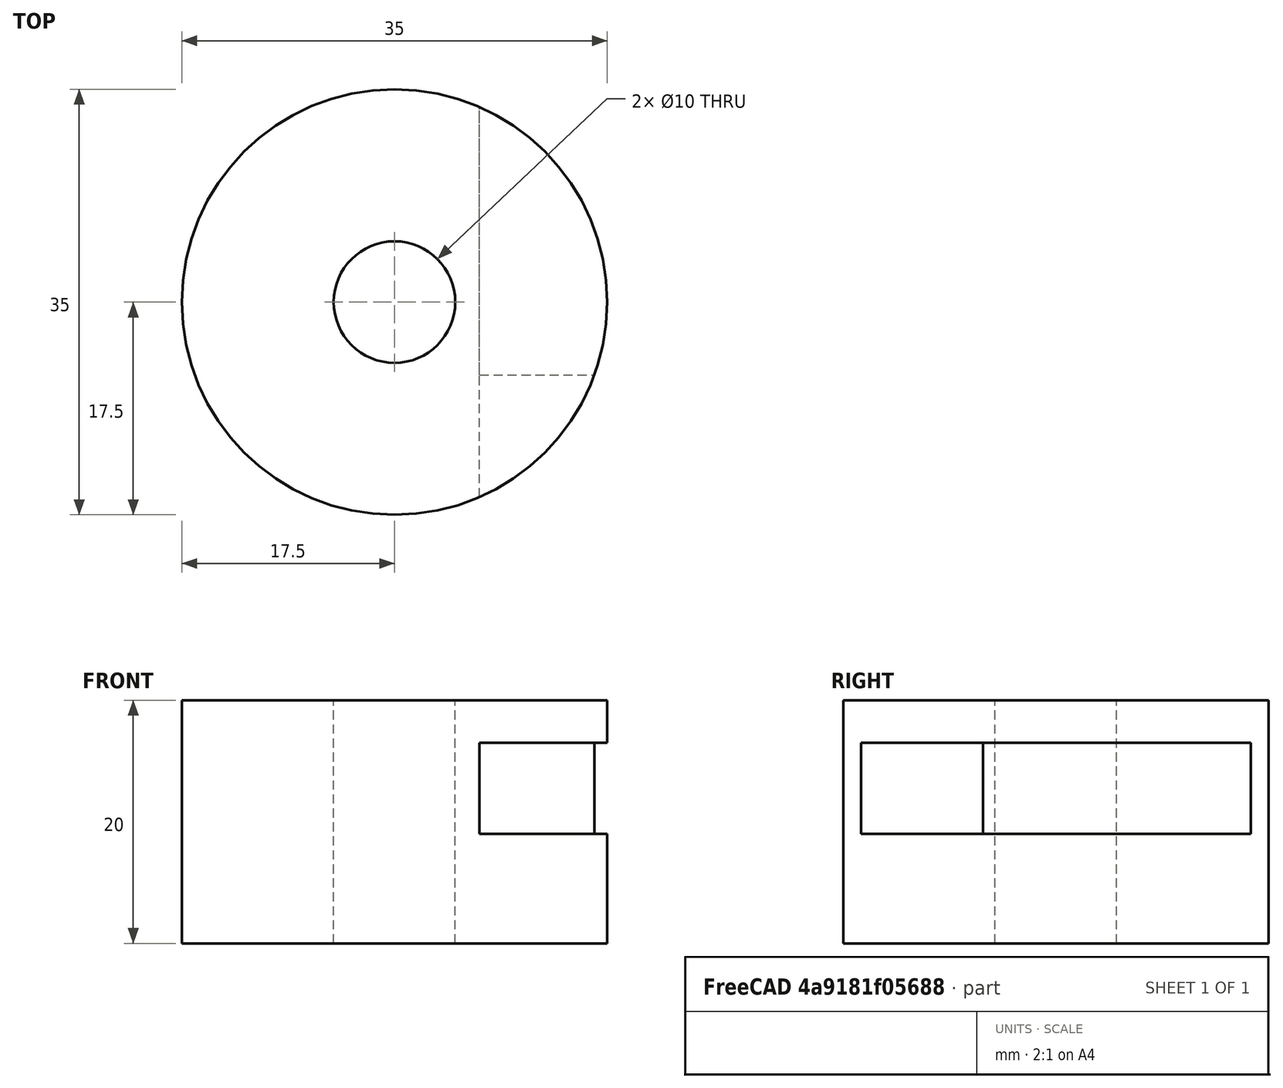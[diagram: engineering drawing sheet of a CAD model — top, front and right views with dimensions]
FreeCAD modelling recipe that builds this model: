
FCSTD DOCUMENT  (FreeCAD 0.15R4671 (Git))
Label: sign-with-hardware
License: All rights reserved
LicenseURL: http://en.wikipedia.org/wiki/All_rights_reserved
objects: Drawing::FeatureView×8, Drawing::FeatureViewPart×6, Part::Cylinder×4, Part::Cut×4, Part::Box×2, Drawing::FeaturePage×1, Mesh::Feature×1
note: 10 computed .brp shape members not serialized (recipe doc carries the construction recipe); baked Part::Feature solids carry a one-line shape summary decoded from their .brp

FEATURE [Part::Cylinder] Cylinder
  Angle = 360
  Height = 20
  Radius = 17.5
FEATURE [Part::Cylinder] Cylinder001
  Angle = 360
  Height = 40
  Placement = pos=(0,0,-10) rot=(0,0,1;0rad)
  Radius = 5
FEATURE [Part::Cut] Cut
  Base = -> Cylinder
  Tool = -> Cylinder001
FEATURE [Part::Box] Box  label="Cube"
  Height = 7.5
  Length = 30
  Placement = pos=(7,-6,9) rot=(0,0,1;0rad)
  Width = 30
FEATURE [Part::Cut] Cut001  label="Mount (Bottom)"
  Base = -> Cut
  Tool = -> Box
FEATURE [Part::Cylinder] Cylinder002
  Angle = 360
  Height = 20
  Radius = 17.5
FEATURE [Part::Cylinder] Cylinder003
  Angle = 360
  Height = 40
  Placement = pos=(0,0,-10) rot=(0,0,1;0rad)
  Radius = 5
FEATURE [Part::Cut] Cut002
  Base = -> Cylinder002
  Tool = -> Cylinder003
FEATURE [Part::Box] Box001  label="Cube001"
  Height = 7.5
  Length = 30
  Placement = pos=(7,-20,9) rot=(0,0,1;0rad)
  Width = 70
FEATURE [Part::Cut] Cut003  label="Mount (Top)"
  Base = -> Cut002
  Tool = -> Box001
FEATURE [Drawing::FeatureViewPart] View  label="Bottom - Front"
  Direction = (0,0,1)
  HiddenWidth = 0.15
  LineWidth = 0.35
  Rotation = 0
  ShowHiddenLines = true
  ShowSmoothLines = false
  Source = -> Cut001
  Tolerance = 0.05
  ViewResult = <g id="Bottom - Front"\n   transform="rotate(0,70,50) translate(70,50) scale(1,1)"\n  >\n<g   stroke="rgb(0, 0, 0)"\n   stroke-width="0.15"\n   stroke-linecap="butt"\n   stroke-linejoin="miter"\n   stroke-dasharray="0.2,0.1"\n   fill="none"\n   transform="scale(1,-1)"\n  >\n<path d="M16.4393 -6 A17.5 17.5 0 0 1 17.5 -4.28626e-015" /><path d="M16.4393 -6 A17.5 17.5 0 0 1 17.5 -4.28626e-015" /><circle cx ="0" cy ="0" r ="17.5" /><path d="M17.5 0 A17.5 17.5 0 0 1 7 16.039" /><path d="M17.5 0 A17.5 17.5 0 0 1 7 16.039" /><path id= "6" d=" M 7 -6 L 7 16.039 " />\n<path id= "7" d=" M 7 -6 L 16.4393 -6 " />\n<path id= "8" d=" M 7 -6 L 16.4393 -6 " />\n<path id= "9" d=" M 7 -6 L 7 16.039 " />\n<circle cx ="0" cy ="0" r ="5" /></g>\n<g   stroke="rgb(0, 0, 0)"\n   stroke-width="0.35"\n   stroke-linecap="butt"\n   stroke-linejoin="miter"\n   fill="none"\n   transform="scale(1,-1)"\n  >\n<circle cx ="0" cy ="0" r ="17.5" /><circle cx ="0" cy ="0" r ="5" /></g>\n</g>
  Visible = true
  X = 70
  Y = 50
FEATURE [Drawing::FeatureViewPart] View001  label="Top - Front"
  Direction = (0,0,1)
  HiddenWidth = 0.15
  LineWidth = 0.35
  Rotation = 0
  ShowHiddenLines = true
  ShowSmoothLines = false
  Source = -> Cut003
  Tolerance = 0.05
  ViewResult = <g id="Top - Front"\n   transform="rotate(0,70,120) translate(70,120) scale(1,1)"\n  >\n<g   stroke="rgb(0, 0, 0)"\n   stroke-width="0.15"\n   stroke-linecap="butt"\n   stroke-linejoin="miter"\n   stroke-dasharray="0.2,0.1"\n   fill="none"\n   transform="scale(1,-1)"\n  >\n<path d="M7 -16.039 A17.5 17.5 0 0 1 17.5 -4.28626e-015" /><path d="M7 -16.039 A17.5 17.5 0 0 1 17.5 -4.28626e-015" /><circle cx ="0" cy ="0" r ="17.5" /><path d="M17.5 0 A17.5 17.5 0 0 1 7 16.039" /><path d="M17.5 0 A17.5 17.5 0 0 1 7 16.039" /><path id= "6" d=" M 7 -16.039 L 7 16.039 " />\n<path id= "7" d=" M 7 -16.039 L 7 16.039 " />\n<circle cx ="0" cy ="0" r ="5" /></g>\n<g   stroke="rgb(0, 0, 0)"\n   stroke-width="0.35"\n   stroke-linecap="butt"\n   stroke-linejoin="miter"\n   fill="none"\n   transform="scale(1,-1)"\n  >\n<circle cx ="0" cy ="0" r ="17.5" /><circle cx ="0" cy ="0" r ="5" /></g>\n</g>
  Visible = true
  X = 70
  Y = 120
FEATURE [Drawing::FeatureViewPart] View002  label="Top - Side"
  Direction = (1,0,0)
  HiddenWidth = 0.15
  LineWidth = 0.35
  Rotation = 180
  ShowHiddenLines = true
  ShowSmoothLines = false
  Source = -> Cut003
  Tolerance = 0.05
  ViewResult = <blob: 4388 chars omitted>
  Visible = true
  X = 160
  Y = 120
FEATURE [Drawing::FeatureViewPart] View003  label="Bottom - Side"
  Direction = (1,0,0)
  HiddenWidth = 0.15
  LineWidth = 0.35
  Rotation = 180
  ShowHiddenLines = false
  ShowSmoothLines = false
  Source = -> Cut001
  Tolerance = 0.05
  ViewResult = <blob: 2232 chars omitted>
  Visible = true
  X = 160
  Y = 50
FEATURE [Drawing::FeatureViewPart] View004  label="Bottom - Ortho"
  Direction = (1,1,1)
  HiddenWidth = 0.15
  LineWidth = 0.35
  Rotation = 0
  ShowHiddenLines = false
  ShowSmoothLines = false
  Source = -> Cut001
  Tolerance = 0.05
  ViewResult = <g id="Bottom - Ortho"\n   transform="rotate(0,240,45) translate(240,45) scale(1,1)"\n  >\n<g   stroke="rgb(0, 0, 0)"\n   stroke-width="0.35"\n   stroke-linecap="butt"\n   stroke-linejoin="miter"\n   fill="none"\n   transform="scale(1,-1)"\n  >\n<path id= "1" d=" M -8.75 15.1554 L -22.8921 6.99048 " />\n<path id= "2" d=" M 8.75 -15.1554 L -5.39214 -23.3204 " />\n</g>\n<g   stroke="rgb(0, 0, 0)"\n   stroke-width="0.35"\n   stroke-linecap="butt"\n   stroke-linejoin="miter"\n   fill="none"\n   transform="scale(1,-1)"\n  >\n<path d="M-0.042934 -18.3464 A17.5 10.1036 120 0 1 0.707107 -13.8804" />\n<path id= "2" d=" M 5.26037 -15.2845 L -0.042934 -18.3464 " />\n<path d="M5.26037 -15.2845 A17.5 10.1036 120 0 1 6.01041 -10.8186" />\n<path d="M12.3744 -7.14435 A17.5 10.1036 120 0 1 -8.75 15.1554" />\n<path d="M8.75 -15.1554 A17.5 10.1036 120 0 1 12.3744 -7.14435" />\n<path d="M6.01041 -10.8186 A17.5 10.1036 120 0 1 -1.41421 6.56383" />\n<path id= "7" d=" M -1.41421 6.56383 L -6.71751 3.50197 " />\n<path d="M0.707107 -13.8804 A17.5 10.1036 120 0 1 -6.71751 3.50197" />\n<path d="M-1.76777 -15.3093 A17.5 10.1036 120 0 1 -22.8921 6.99048" />\n<path d="M-22.8921 6.99048 A17.5 10.1036 120 0 1 -5.39214 -23.3204" />\n<path d="M-5.39214 -23.3204 A17.5 10.1036 120 0 1 -1.76777 -15.3093" />\n<path id= "12" d=" M 0.661566 -12.6294 L 5.26037 -15.2845 " />\n<path id= "13" d=" M -1.41421 -4.6557 L -1.41421 6.56383 " />\n<path d="M-10.6066 -10.2062 A5 2.88675 120 0 1 -16.6421 -3.83484" />\n<path d="M-16.6421 -3.83484 A5 2.88675 120 0 1 -11.6421 -12.4951" />\n<path d="M-11.6421 -12.4951 A5 2.88675 120 0 1 -10.6066 -10.2062" />\n</g>\n</g>
  Visible = true
  X = 240
  Y = 45
FEATURE [Drawing::FeatureViewPart] View005  label="Top - Ortho"
  Direction = (1,1,1)
  HiddenWidth = 0.15
  LineWidth = 0.35
  Rotation = 0
  ShowHiddenLines = false
  ShowSmoothLines = false
  Source = -> Cut003
  Tolerance = 0.05
  ViewResult = <g id="Top - Ortho"\n   transform="rotate(0,240,115) translate(240,115) scale(1,1)"\n  >\n<g   stroke="rgb(0, 0, 0)"\n   stroke-width="0.35"\n   stroke-linecap="butt"\n   stroke-linejoin="miter"\n   fill="none"\n   transform="scale(1,-1)"\n  >\n<path id= "1" d=" M -8.75 15.1554 L -22.8921 6.99048 " />\n<path id= "2" d=" M 8.75 -15.1554 L 2.38604 -18.8297 " />\n<path id= "3" d=" M -2.91726 -21.8915 L -5.39214 -23.3204 " />\n</g>\n<g   stroke="rgb(0, 0, 0)"\n   stroke-width="0.35"\n   stroke-linecap="butt"\n   stroke-linejoin="miter"\n   fill="none"\n   transform="scale(1,-1)"\n  >\n<path d="M-2.91726 -21.8915 A17.5 10.1036 120 0 1 0.707107 -13.8804" />\n<path d="M-0.677071 -19.6479 A17.5 10.1036 120 0 1 2.38604 -18.8297" />\n<path d="M2.38604 -18.8297 A17.5 10.1036 120 0 1 6.01041 -10.8186" />\n<path d="M12.3744 -7.14435 A17.5 10.1036 120 0 1 -8.75 15.1554" />\n<path d="M8.75 -15.1554 A17.5 10.1036 120 0 1 12.3744 -7.14435" />\n<path d="M6.01041 -10.8186 A17.5 10.1036 120 0 1 -1.41421 6.56383" />\n<path id= "7" d=" M -1.41421 6.56383 L -6.71751 3.50197 " />\n<path d="M0.707107 -13.8804 A17.5 10.1036 120 0 1 -6.71751 3.50197" />\n<path d="M-1.76777 -15.3093 A17.5 10.1036 120 0 1 -22.8921 6.99048" />\n<path d="M-22.8921 6.99048 A17.5 10.1036 120 0 1 -5.39214 -23.3204" />\n<path d="M-5.39214 -23.3204 A17.5 10.1036 120 0 1 -1.76777 -15.3093" />\n<path id= "12" d=" M -1.41421 -4.6557 L -1.41421 6.56383 " />\n<path d="M-10.6066 -10.2062 A5 2.88675 120 0 1 -16.6421 -3.83484" />\n<path d="M-16.6421 -3.83484 A5 2.88675 120 0 1 -11.6421 -12.4951" />\n<path d="M-11.6421 -12.4951 A5 2.88675 120 0 1 -10.6066 -10.2062" />\n</g>\n</g>
  Visible = true
  X = 240
  Y = 115
FEATURE [Drawing::FeatureView] dim
  Rotation = 0
  ViewResult = <g>  <circle cx ="70.000000" cy ="50.000000" r="0.500000" stroke="none" fill="rgb(0,0,0)" /> \n<line x1="42.768659" y1="28.041715" x2="70.000000" y2="50.000000" style="stroke:rgb(0,0,0);stroke-width:0.30" />\n<polygon points="56.377167,39.015082 58.084800,41.676658 59.490957,41.525920 59.340219,40.119763" style="fill:rgb(0,0,0);stroke:rgb(0,0,0);stroke-width:0" />\n<line x1="42.768659" y1="28.041715" x2="32.076494" y2="28.041715" style="stroke:rgb(0,0,0);stroke-width:0.30" />\n<text x="37.422577" y="26.041715" font-family="arial" font-size="3.6" fill="rgb(0,0,0)" text-anchor="middle" transform="rotate(0.000000 37.422577,26.041715)" >R17.5</text> </g>
  Visible = true
  X = 0
  Y = 0
FEATURE [Drawing::FeatureView] dim001
  Rotation = 0
  ViewResult = <g> \n  <line x1="72.000000" y1="32.500000" x2="104.804067" y2="32.500000" style="stroke:rgb(0,0,0);stroke-width:0.30" />\n<line x1="88.439300" y1="56.000000" x2="104.804067" y2="56.000000" style="stroke:rgb(0,0,0);stroke-width:0.30" />\n<line x1="103.804067" y1="32.500000" x2="103.804067" y2="56.000000" style="stroke:rgb(0,0,0);stroke-width:0.30" /> \n  <polygon points="103.804067,56.000000 104.804067,53.000000 103.804067,52.000000 102.804067,53.000000" style="fill:rgb(0,0,0);stroke:rgb(0,0,0);stroke-width:0" /><polygon points="103.804067,32.500000 102.804067,35.500000 103.804067,36.500000 104.804067,35.500000" style="fill:rgb(0,0,0);stroke:rgb(0,0,0);stroke-width:0" /> \n  <text x="101.804067" y="44.250000" font-family="arial" font-size="3.6" fill="rgb(0,0,0)" text-anchor="middle" transform="rotate(-90.000000 101.804067,44.250000)" >23.5</text> </g>
  Visible = true
  X = 0
  Y = 0
FEATURE [Drawing::FeatureView] dim002
  Rotation = 0
  ViewResult = <g> \n  <line x1="70.000000" y1="69.500000" x2="70.000000" y2="80.081671" style="stroke:rgb(0,0,0);stroke-width:0.30" />\n<line x1="77.000000" y1="58.000000" x2="77.000000" y2="80.081671" style="stroke:rgb(0,0,0);stroke-width:0.30" />\n<line x1="70.000000" y1="79.081671" x2="77.000000" y2="79.081671" style="stroke:rgb(0,0,0);stroke-width:0.30" /> \n  <polygon points="77.000000,79.081671 80.000000,80.081671 81.000000,79.081671 80.000000,78.081671" style="fill:rgb(0,0,0);stroke:rgb(0,0,0);stroke-width:0" /><polygon points="70.000000,79.081671 67.000000,78.081671 66.000000,79.081671 67.000000,80.081671" style="fill:rgb(0,0,0);stroke:rgb(0,0,0);stroke-width:0" /> \n  <text x="73.500000" y="77.081671" font-family="arial" font-size="3.6" fill="rgb(0,0,0)" text-anchor="middle" transform="rotate(0.000000 73.500000,77.081671)" >7</text> </g>
  Visible = true
  X = 0
  Y = 0
FEATURE [Drawing::FeatureView] centerLines
  Rotation = 0
  ViewResult = <g transform="scale(1.000000,1.000000)" stroke="rgb(0,0,0)"  stroke-width="0.300000" > <path d="M 70.000000,50.000000 L 70.000000,52.000000 M 70.000000,54.000000 L 70.000000,60.000000 "/>\n<path d="M 70.000000,50.000000 L 72.000000,50.000000 M 74.000000,50.000000 L 80.000000,50.000000 "/>\n<path d="M 70.000000,50.000000 L 70.000000,48.000000 M 70.000000,46.000000 L 70.000000,40.000000 "/>\n<path d="M 70.000000,50.000000 L 68.000000,50.000000 M 66.000000,50.000000 L 60.000000,50.000000 "/> </g> 
  Visible = true
  X = 0
  Y = 0
FEATURE [Drawing::FeatureView] centerLines001
  Rotation = 0
  ViewResult = <g transform="scale(1.000000,1.000000)" stroke="rgb(0,0,0)"  stroke-width="0.300000" > <path d="M 70.000000,120.000000 L 70.000000,118.000000 M 70.000000,116.000000 L 70.000000,110.000000 "/>\n<path d="M 70.000000,120.000000 L 68.000000,120.000000 M 66.000000,120.000000 L 60.000000,120.000000 "/>\n<path d="M 70.000000,120.000000 L 70.000000,122.000000 M 70.000000,124.000000 L 70.000000,130.000000 "/>\n<path d="M 70.000000,120.000000 L 72.000000,120.000000 M 74.000000,120.000000 L 80.000000,120.000000 "/> </g> 
  Visible = true
  X = 0
  Y = 0
FEATURE [Drawing::FeatureView] dim003
  Rotation = 0
  ViewResult = <g> \n  <line x1="140.000000" y1="69.500000" x2="140.000000" y2="80.303158" style="stroke:rgb(0,0,0);stroke-width:0.30" />\n<line x1="160.000000" y1="69.500000" x2="160.000000" y2="80.303158" style="stroke:rgb(0,0,0);stroke-width:0.30" />\n<line x1="140.000000" y1="79.303158" x2="160.000000" y2="79.303158" style="stroke:rgb(0,0,0);stroke-width:0.30" /> \n  <polygon points="160.000000,79.303158 157.000000,78.303158 156.000000,79.303158 157.000000,80.303158" style="fill:rgb(0,0,0);stroke:rgb(0,0,0);stroke-width:0" /><polygon points="140.000000,79.303158 143.000000,80.303158 144.000000,79.303158 143.000000,78.303158" style="fill:rgb(0,0,0);stroke:rgb(0,0,0);stroke-width:0" /> \n  <text x="150.000000" y="77.303158" font-family="arial" font-size="3.6" fill="rgb(0,0,0)" text-anchor="middle" transform="rotate(0.000000 150.000000,77.303158)" >20</text> </g>
  Visible = true
  X = 0
  Y = 0
FEATURE [Drawing::FeatureView] dim004
  Rotation = 0
  ViewResult = <g> \n  <line x1="143.500000" y1="101.961000" x2="143.500000" y2="93.649391" style="stroke:rgb(0,0,0);stroke-width:0.30" />\n<line x1="151.000000" y1="101.961000" x2="151.000000" y2="93.649391" style="stroke:rgb(0,0,0);stroke-width:0.30" />\n<line x1="143.500000" y1="94.649391" x2="151.000000" y2="94.649391" style="stroke:rgb(0,0,0);stroke-width:0.30" /> \n  <polygon points="151.000000,94.649391 154.000000,95.649391 155.000000,94.649391 154.000000,93.649391" style="fill:rgb(0,0,0);stroke:rgb(0,0,0);stroke-width:0" /><polygon points="143.500000,94.649391 140.500000,93.649391 139.500000,94.649391 140.500000,95.649391" style="fill:rgb(0,0,0);stroke:rgb(0,0,0);stroke-width:0" /> \n  <text x="147.250000" y="92.649391" font-family="arial" font-size="3.6" fill="rgb(0,0,0)" text-anchor="middle" transform="rotate(0.000000 147.250000,92.649391)" >7.5</text> </g>
  Visible = true
  X = 0
  Y = 0
FEATURE [Drawing::FeatureView] dim005
  Rotation = 0
  ViewResult = <g> \n  <line x1="87.500000" y1="118.000000" x2="87.500000" y2="93.996707" style="stroke:rgb(0,0,0);stroke-width:0.30" />\n<line x1="77.000000" y1="101.961000" x2="77.000000" y2="93.996707" style="stroke:rgb(0,0,0);stroke-width:0.30" />\n<line x1="87.500000" y1="94.996707" x2="77.000000" y2="94.996707" style="stroke:rgb(0,0,0);stroke-width:0.30" /> \n  <polygon points="77.000000,94.996707 80.000000,95.996707 81.000000,94.996707 80.000000,93.996707" style="fill:rgb(0,0,0);stroke:rgb(0,0,0);stroke-width:0" /><polygon points="87.500000,94.996707 84.500000,93.996707 83.500000,94.996707 84.500000,95.996707" style="fill:rgb(0,0,0);stroke:rgb(0,0,0);stroke-width:0" /> \n  <text x="82.250000" y="92.996707" font-family="arial" font-size="3.6" fill="rgb(0,0,0)" text-anchor="middle" transform="rotate(0.000000 82.250000,92.996707)" >10.5</text> </g>
  Visible = true
  X = 0
  Y = 0
FEATURE [Drawing::FeaturePage] Page  label="Drawing"
  EditableTexts = FLOYD DIEBEL | 02/02/2016 | 1:1 | GROUNDED SIGN | Slotted Standoff Hardware | 01 | 02
  Group = -> [View,View003,View004,View005,View002,View001,dim,dim001,dim002,centerLines,centerLines001,dim003,dim004,dim005]
  Template = D:/Program Files/FreeCAD 0.15/data/Mod/Drawing/Templates/A4_Landscape.svg
FEATURE [Mesh::Feature] sign_plate  label="sign-plate"
